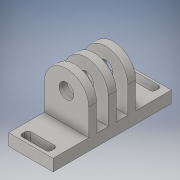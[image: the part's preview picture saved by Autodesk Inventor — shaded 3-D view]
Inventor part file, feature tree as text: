
AUTODESK INVENTOR PART (.ipt)
format: ipt  version: 2016 (Build 200138000, 138)  size: 189,952 bytes
history: native  units: in
note: dims shown in document units (in); Inventor stores cm internally (conversion verified against a paired STEP export)
features: extrude x3, sketch x3, fillet x1
ambient origin geometry x8: Origin, YZ Plane, XZ Plane, XY Plane, X Axis, Y Axis, Z Axis, Center Point
bodies: Solid1 (feature_tree)
feature tree (7):
  extrude  "Extrusion1"  Depth=0.2953in
  fillet  "Fillet1"  Radius=0.6496in
  extrude  "Extrusion5"  Depth=0.2559in
  extrude  "Extrusion8"  Depth=0.2953in
  sketch  "Sketch4"  dims[d0=0.2953in d1=0.2953in d2=0.6496in]
  sketch  "Sketch10"  dims[d3=0.1969in d4=0.2559in]
  sketch  "Sketch13"  dims[d5=0.626in d6=0.0in d7=0.2953in d20=0.5906in d21=1.5748in d22=0.4744in d23=0.2953in d24=0.1181in d25=0.0394in d26=0.3937in d27=0.0984in d28=0.3179in d29=0.0394in d30=0.1575in d31=0.0in d47=0.1063in d48=0.1063in d49=0.1063in d50=0.626in d51=0.1535in d52=0.1535in d53=1.0in d54=0.0in]
